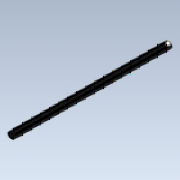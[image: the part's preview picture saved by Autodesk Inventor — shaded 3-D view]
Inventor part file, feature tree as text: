
AUTODESK INVENTOR PART (.ipt)
format: ipt  version: 2020 (Build 240168000, 168)  size: 117,248 bytes
history: native  units: in
note: dims shown in document units (in); Inventor stores cm internally (conversion verified against a paired STEP export)
features: extrude x1, sketch x1
ambient origin geometry x8: Origin, YZ Plane, XZ Plane, XY Plane, X Axis, Y Axis, Z Axis, Center Point
bodies: Solid1 (feature_tree)
feature tree (2):
  extrude  "Extrusion1"  Depth=0.5in
  sketch  "Sketch1"  dims[d1=0.5414in d2=0.5in d3=0.2707in d4=0.201in d5=4.0in d6=0.0in d9=0.0in]
